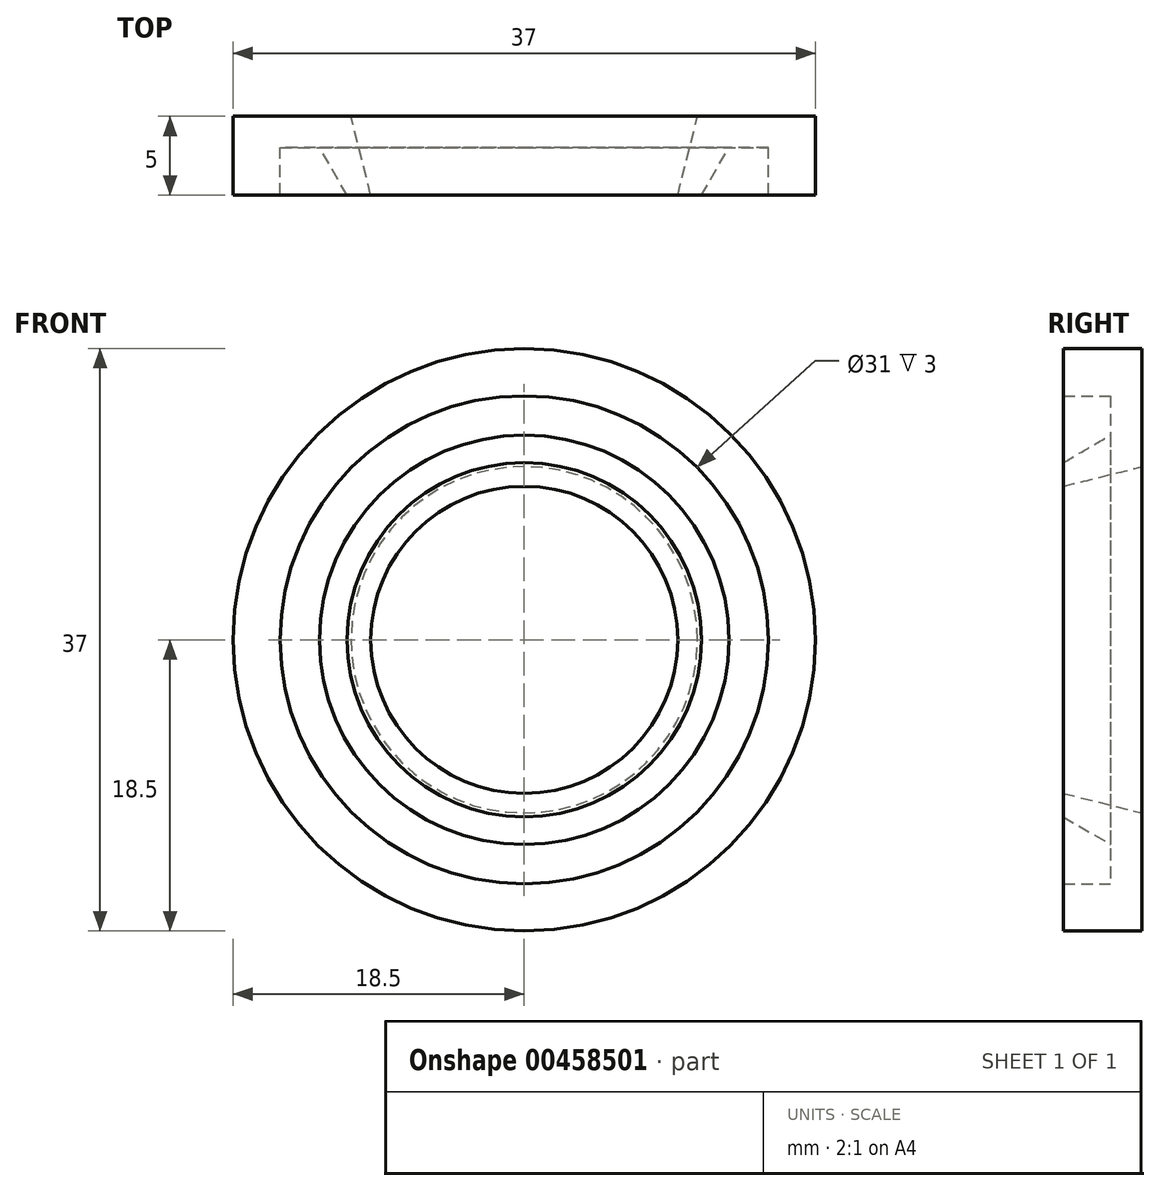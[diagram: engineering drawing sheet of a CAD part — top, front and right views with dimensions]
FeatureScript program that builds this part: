
annotation { "Feature Type Name" : "Feature", "Feature Type Description" : "" }
export const myFeature = defineFeature(function(context is Context, id is Id, definition is map)
    precondition{}
    {
        {
            var Q0;
            Q0=qCreatedBy(makeId("Right.planeOp"),FACE);
            var sketch = newSketch(context, id + "F0", { "sketchPlane" : qUnion([Q0])});
            skLineSegment(sketch, "E0", {"start": v(0, 0) * mm, "end": v(-42.7, 0) * mm, "construction": true});
            skLineSegment(sketch, "E1", {"start": v(0, 0) * mm, "end": v(0, 11) * mm, "construction": true});
            skLineSegment(sketch, "E2", {"start": v(0, 11) * mm, "end": v(0, 18.5) * mm, "construction": true});
            skLineSegment(sketch, "E3", {"start": v(0, 18.5) * mm, "end": v(-2, 18.5) * mm, "construction": true});
            skLineSegment(sketch, "E4", {"start": v(-2, 18.5) * mm, "end": v(-5, 18.5) * mm, "construction": true});
            skLineSegment(sketch, "E5", {"start": v(-5, 18.5) * mm, "end": v(-5, 15.5) * mm, "construction": true});
            skLineSegment(sketch, "E6", {"start": v(0, 0) * mm, "end": v(0, 14.75) * mm, "construction": true});
            skLineSegment(sketch, "E7", {"start": v(-5, 15.5) * mm, "end": v(-2, 15.5) * mm});
            skLineSegment(sketch, "E8", {"start": v(-2, 15.5) * mm, "end": v(-2, 13) * mm});
            skLineSegment(sketch, "E9", {"start": v(-5, 15.5) * mm, "end": v(-5, 11.25) * mm, "construction": true});
            skLineSegment(sketch, "E10", {"start": v(-5, 11.25) * mm, "end": v(-2, 13) * mm, "construction": true});
            skLineSegment(sketch, "E11", {"start": v(-5, 11.25) * mm, "end": v(-5, 9.75) * mm, "construction": true});
            skLineSegment(sketch, "E12", {"start": v(-5, 11.25) * mm, "end": v(-5, 9.75) * mm});
            skLineSegment(sketch, "E13", {"start": v(-5, 9.75) * mm, "end": v(0, 11) * mm, "construction": true});
            skLineSegment(sketch, "E14", {"start": v(-5, 18.5) * mm, "end": v(-5, 15.5) * mm});
            skLineSegment(sketch, "E15", {"start": v(-2, 15.5) * mm, "end": v(-5, 15.5) * mm});
            skLineSegment(sketch, "E16", {"start": v(-2, 13) * mm, "end": v(-5, 11.25) * mm});
            skLineSegment(sketch, "E17", {"start": v(-5, 9.75) * mm, "end": v(0, 11) * mm});
            skLineSegment(sketch, "E18", {"start": v(0, 11) * mm, "end": v(0, 18.5) * mm});
            skLineSegment(sketch, "E19", {"start": v(0, 18.5) * mm, "end": v(-5, 18.5) * mm});
            skSolve(sketch);
        }
        {
            var Q0;
            Q0=makeQuery(id+"F0.imprint","IMPRINT",FACE,{"disambiguationData":[TD([[makeQuery(id+"F0.imprint","IMPRINT",EDGE,{"derivedFrom":sQuery(id+"F0.wireOp",EDGE,"E14")}),1.0]])]});
            var Q1;
            Q1=sQuery(id+"F0.wireOp",EDGE,"E0");
            revolve(context, id + "F1", {"entities" : qUnion([Q0]), "axis" : qUnion([Q1]), "revolveType" : RevolveType.FULL});
        }
    });
